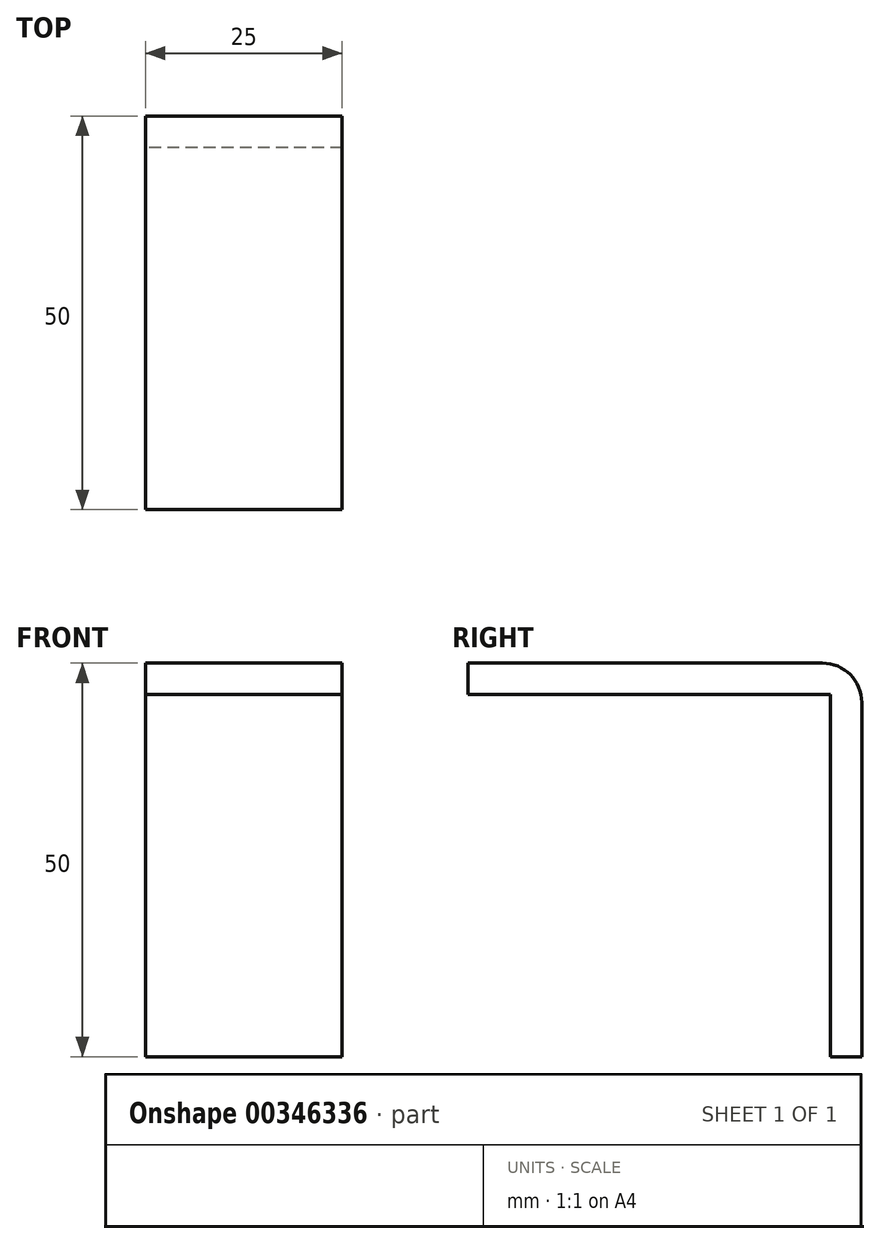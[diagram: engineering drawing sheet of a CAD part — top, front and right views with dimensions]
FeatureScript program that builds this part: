
annotation { "Feature Type Name" : "Feature", "Feature Type Description" : "" }
export const myFeature = defineFeature(function(context is Context, id is Id, definition is map)
    precondition{}
    {
        {
            var Q0;
            Q0=qCreatedBy(makeId("Right.planeOp"),FACE);
            var sketch = newSketch(context, id + "F0", { "sketchPlane" : qUnion([Q0])});
            skLineSegment(sketch, "E0", {"start": v(-46.83, 0) * mm, "end": v(3.17, 0) * mm});
            skLineSegment(sketch, "E1", {"start": v(3.17, -50) * mm, "end": v(3.17, 0) * mm});
            skLineSegment(sketch, "E2", {"start": v(3.17, -50) * mm, "end": v(-0.83, -50) * mm});
            skLineSegment(sketch, "E3", {"start": v(-0.83, 0) * mm, "end": v(-0.83, -50) * mm});
            skLineSegment(sketch, "E4", {"start": v(-46.83, 0) * mm, "end": v(-46.83, -4) * mm});
            skLineSegment(sketch, "E5", {"start": v(3.17, -4) * mm, "end": v(-46.83, -4) * mm});
            skSolve(sketch);
        }
        {
            var Q0;
            Q0 = qSketchRegion(id + "F0", true);
            extrude(context, id + "F1", {"entities" : qUnion([Q0]), "depth" : 25 * mm});
        }
        {
            var Q0;
            Q0=makeQuery(id+"F1.opExtrude","SWEPT_EDGE",EDGE,{"disambiguationData":[OSD([sQuery(id+"F0.wireOp",EDGE,"E0"),sQuery(id+"F0.wireOp",EDGE,"E1")])]});
            fillet(context, id + "F2", {"entities" : qUnion([Q0]), "radius" : 5 * mm, "tangentPropagation" : true, "allowEdgeOverflow" : false});
        }
    });
